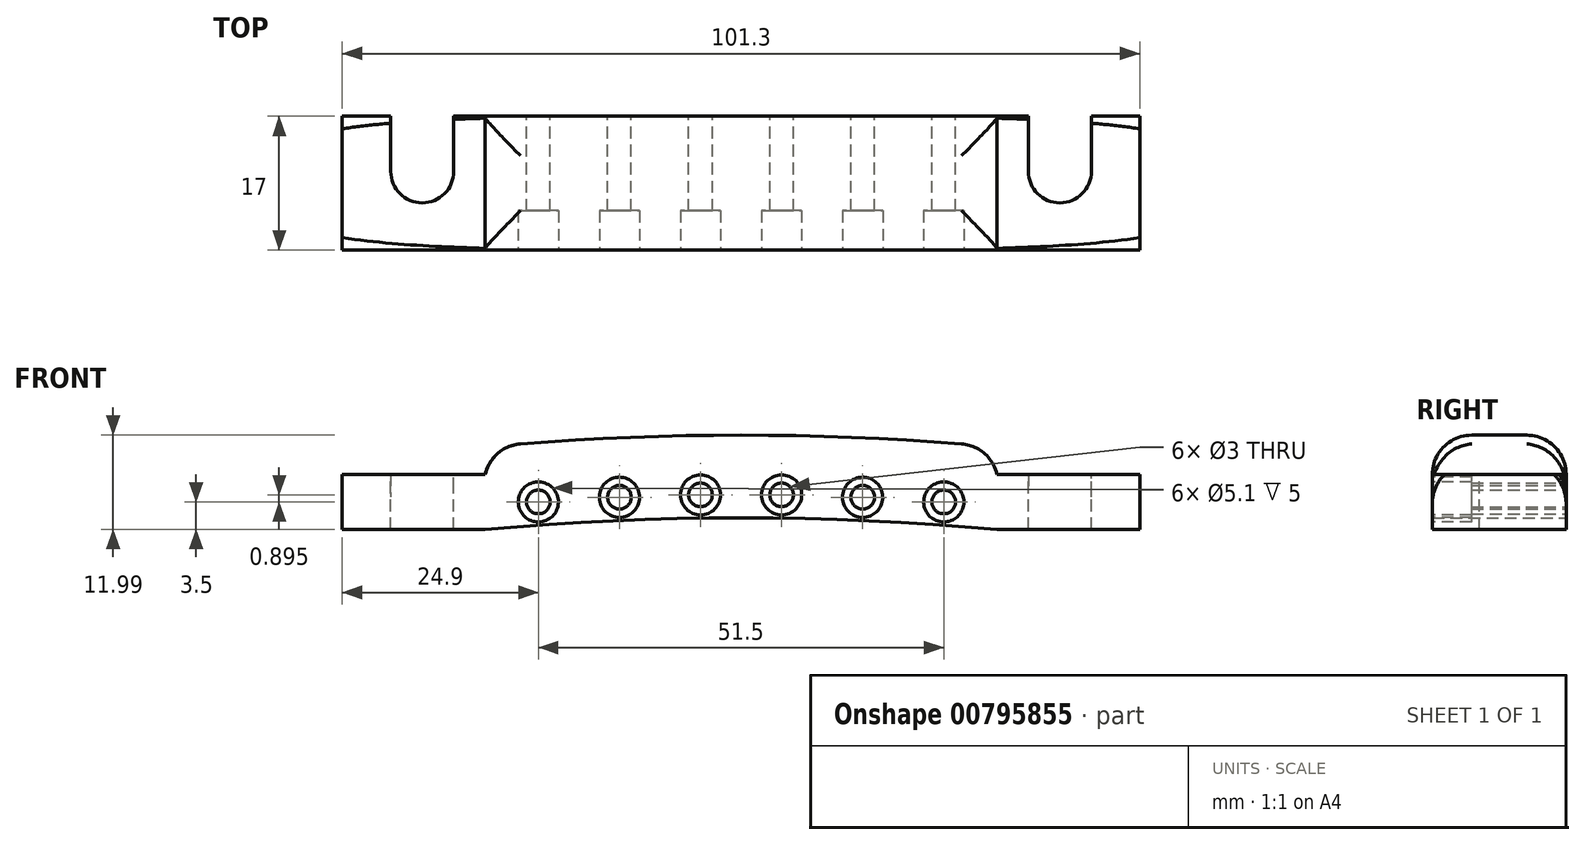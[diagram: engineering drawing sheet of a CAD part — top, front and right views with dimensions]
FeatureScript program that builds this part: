
annotation { "Feature Type Name" : "Feature", "Feature Type Description" : "" }
export const myFeature = defineFeature(function(context is Context, id is Id, definition is map)
    precondition{}
    {
        {
            var Q0;
            Q0=qCreatedBy(makeId("Front.planeOp"),FACE);
            var sketch = newSketch(context, id + "F0", { "sketchPlane" : qUnion([Q0])});
            skLineSegment(sketch, "E0", {"start": v(-50.65, 3.5) * mm, "end": v(-50.65, -3.5) * mm});
            skLineSegment(sketch, "E1", {"start": v(-50.65, -3.5) * mm, "end": v(-32.5, -3.5) * mm});
            skLineSegment(sketch, "E2", {"start": v(-50.65, 3.5) * mm, "end": v(-32.5, 3.5) * mm});
            skLineSegment(sketch, "E3", {"start": v(32.5, 3.5) * mm, "end": v(50.65, 3.5) * mm});
            skLineSegment(sketch, "E4", {"start": v(50.65, 3.5) * mm, "end": v(50.65, -3.5) * mm});
            skLineSegment(sketch, "E5", {"start": v(50.65, -3.5) * mm, "end": v(32.5, -3.5) * mm});
            skArc(sketch, "E6", {"start": v(-32.5, -3.5) * mm, "mid": v(0, -2.01) * mm, "end": v(32.5, -3.5) * mm});
            skArc(sketch, "E7", {"start": v(-32.5, 3.5) * mm, "mid": v(0, 4.99) * mm, "end": v(32.5, 3.5) * mm, "construction": true});
            skArc(sketch, "E8", {"start": v(-25.75, 0) * mm, "mid": v(0, 0.93) * mm, "end": v(25.75, 0) * mm, "construction": true});
            skCircle(sketch, "E9", {"center": v(-25.75, 0) * mm, "radius": 1.5 * mm});
            skCircle(sketch, "E10", {"center": v(-15.45, 0.6) * mm, "radius": 1.5 * mm});
            skCircle(sketch, "E11", {"center": v(-5.15, 0.9) * mm, "radius": 1.5 * mm});
            skCircle(sketch, "E12", {"center": v(5.15, 0.9) * mm, "radius": 1.5 * mm});
            skCircle(sketch, "E13", {"center": v(15.45, 0.6) * mm, "radius": 1.5 * mm});
            skCircle(sketch, "E14", {"center": v(25.75, 0) * mm, "radius": 1.5 * mm});
            skArc(sketch, "E15", {"start": v(-32.5, 7) * mm, "mid": v(0, 8.49) * mm, "end": v(32.5, 7) * mm});
            skLineSegment(sketch, "E16", {"start": v(32.5, 3.5) * mm, "end": v(32.5, 7) * mm});
            skLineSegment(sketch, "E17", {"start": v(-32.5, 3.5) * mm, "end": v(-32.5, 7) * mm});
            skSolve(sketch);
        }
        {
            var Q0;
            Q0 = qSketchRegion(id + "F0", true);
            extrude(context, id + "F1", {"entities" : qUnion([Q0]), "depth" : 17 * mm, "offsetDistance" : 25 * mm});
        }
        {
            var Q0;
            Q0=makeQuery(id+"F1.opExtrude","SWEPT_FACE",FACE,{"disambiguationData":[OSD([sQuery(id+"F0.wireOp",EDGE,"E15")])]});
            fillet(context, id + "F2", {"entities" : qUnion([Q0]), "radius" : 5 * mm, "tangentPropagation" : true, "allowEdgeOverflow" : false});
        }
        {
            var Q0;
            Q0=qCreatedBy(makeId("Top.planeOp"),FACE);
            var sketch = newSketch(context, id + "F3", { "sketchPlane" : qUnion([Q0])});
            skCircle(sketch, "E18", {"center": v(40.5, -7) * mm, "radius": 4 * mm});
            skCircle(sketch, "E19", {"center": v(-40.5, -7) * mm, "radius": 4 * mm});
            skLineSegment(sketch, "E20", {"start": v(-44.5, -7) * mm, "end": v(-44.5, 0) * mm});
            skLineSegment(sketch, "E21", {"start": v(-44.5, 0) * mm, "end": v(-36.5, 0) * mm});
            skLineSegment(sketch, "E22", {"start": v(-36.5, 0) * mm, "end": v(-36.5, -7) * mm});
            skLineSegment(sketch, "E23", {"start": v(36.5, -7) * mm, "end": v(36.5, 0) * mm});
            skLineSegment(sketch, "E24", {"start": v(36.5, 0) * mm, "end": v(44.5, 0) * mm});
            skLineSegment(sketch, "E25", {"start": v(44.5, 0) * mm, "end": v(44.5, -7) * mm});
            skSolve(sketch);
        }
        {
            var Q0;
            Q0 = qSketchRegion(id + "F3", true);
            extrude(context, id + "F4", {"entities" : qUnion([Q0]), "operationType" : NewBodyOperationType.REMOVE, "endBound" : BoundingType.SYMMETRIC, "oppositeDirection" : true, "depth" : 25 * mm, "offsetDistance" : 25 * mm});
        }
        {
            var Q0;
            Q0=makeQuery(id+"F1.opExtrude","CAP_FACE",FACE,{"disambiguationData":[OSD([sQuery(id+"F0.wireOp",EDGE,"E0"),sQuery(id+"F0.wireOp",EDGE,"E1"),sQuery(id+"F0.wireOp",EDGE,"E2"),sQuery(id+"F0.wireOp",EDGE,"E3"),sQuery(id+"F0.wireOp",EDGE,"E4"),sQuery(id+"F0.wireOp",EDGE,"E5"),sQuery(id+"F0.wireOp",EDGE,"E6"),sQuery(id+"F0.wireOp",EDGE,"E9"),sQuery(id+"F0.wireOp",EDGE,"E10"),sQuery(id+"F0.wireOp",EDGE,"E11"),sQuery(id+"F0.wireOp",EDGE,"E12"),sQuery(id+"F0.wireOp",EDGE,"E13"),sQuery(id+"F0.wireOp",EDGE,"E14"),sQuery(id+"F0.wireOp",EDGE,"E15"),sQuery(id+"F0.wireOp",EDGE,"E16"),sQuery(id+"F0.wireOp",EDGE,"E17")])],"isStart":false});
            var sketch = newSketch(context, id + "F5", { "sketchPlane" : qUnion([Q0])});
            skCircle(sketch, "E26", {"center": v(-25.75, 0) * mm, "radius": 2.55 * mm});
            skCircle(sketch, "E27", {"center": v(-15.45, 0.6) * mm, "radius": 2.55 * mm});
            skCircle(sketch, "E28", {"center": v(-5.15, 0.9) * mm, "radius": 2.55 * mm});
            skCircle(sketch, "E29", {"center": v(5.15, 0.9) * mm, "radius": 2.55 * mm});
            skCircle(sketch, "E30", {"center": v(15.45, 0.6) * mm, "radius": 2.55 * mm});
            skCircle(sketch, "E31", {"center": v(25.75, 0) * mm, "radius": 2.55 * mm});
            skSolve(sketch);
        }
        {
            var Q0;
            Q0 = qSketchRegion(id + "F5", true);
            extrude(context, id + "F6", {"entities" : qUnion([Q0]), "operationType" : NewBodyOperationType.REMOVE, "oppositeDirection" : true, "depth" : 5 * mm, "offsetDistance" : 25 * mm});
        }
    });
